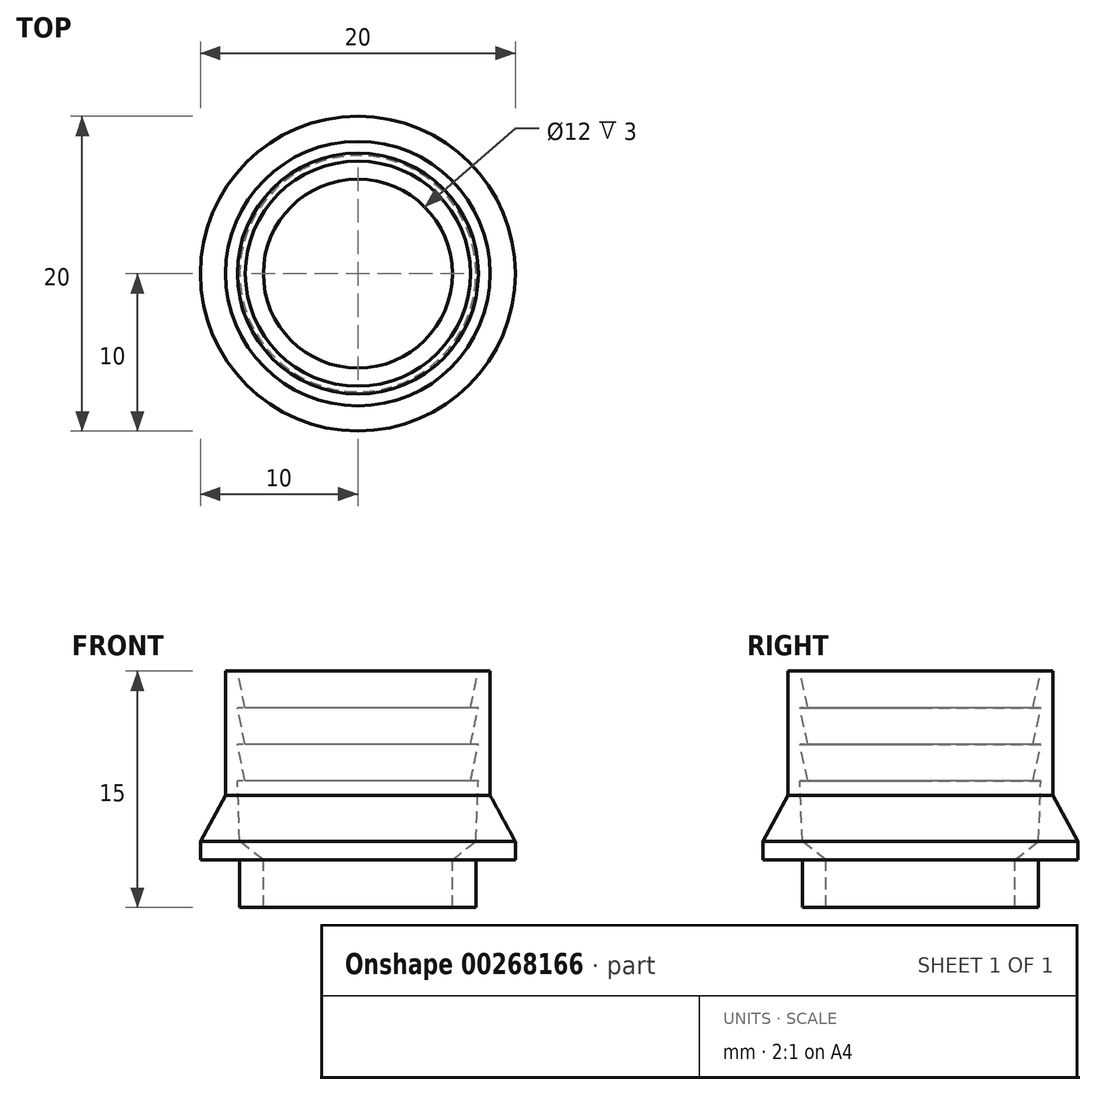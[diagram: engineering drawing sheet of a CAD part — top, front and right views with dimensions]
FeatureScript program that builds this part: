
annotation { "Feature Type Name" : "Feature", "Feature Type Description" : "" }
export const myFeature = defineFeature(function(context is Context, id is Id, definition is map)
    precondition{}
    {
        {
            var Q0;
            Q0=qCreatedBy(makeId("Top.planeOp"),FACE);
            var sketch = newSketch(context, id + "F0", { "sketchPlane" : qUnion([Q0])});
            skCircle(sketch, "E0", {"center": v(0, 0) * mm, "radius": 2.5 * mm});
            skCircle(sketch, "E1", {"center": v(0, 0) * mm, "radius": 4 * mm});
            skCircle(sketch, "E2", {"center": v(0, 0) * mm, "radius": 6 * mm});
            skCircle(sketch, "E3", {"center": v(0, 0) * mm, "radius": 7.5 * mm});
            skSolve(sketch);
        }
        {
            var Q0;
            Q0=qCreatedBy(makeId("Front.planeOp"),FACE);
            var sketch = newSketch(context, id + "F1", { "sketchPlane" : qUnion([Q0])});
            skLineSegment(sketch, "E4", {"start": v(-7.65, 12) * mm, "end": v(-7.15, 9.67) * mm});
            skLineSegment(sketch, "E5", {"start": v(-7.15, 9.67) * mm, "end": v(-7.65, 9.67) * mm});
            skLineSegment(sketch, "E6", {"start": v(-7.65, 9.67) * mm, "end": v(-7.15, 7.35) * mm});
            skLineSegment(sketch, "E7", {"start": v(-7.15, 7.35) * mm, "end": v(-7.65, 7.35) * mm});
            skLineSegment(sketch, "E8", {"start": v(-7.65, 7.35) * mm, "end": v(-7.15, 5.02) * mm});
            skLineSegment(sketch, "E9", {"start": v(-7.15, 5.02) * mm, "end": v(-7.65, 5.02) * mm});
            skLineSegment(sketch, "E10", {"start": v(-7.65, 5.02) * mm, "end": v(-7.5, 1.2) * mm});
            skLineSegment(sketch, "E11", {"start": v(0, 13.24) * mm, "end": v(0, 0) * mm});
            skLineSegment(sketch, "E12", {"start": v(0, 1.2) * mm, "end": v(0, 12) * mm});
            skLineSegment(sketch, "E13", {"start": v(-7.65, 12) * mm, "end": v(-8.4, 12) * mm});
            skLineSegment(sketch, "E14", {"start": v(-10, 1.2) * mm, "end": v(-10, 0) * mm});
            skLineSegment(sketch, "E15", {"start": v(-10, 0) * mm, "end": v(-7.5, 0) * mm});
            skLineSegment(sketch, "E16", {"start": v(-7.5, 0) * mm, "end": v(-7.5, -3) * mm});
            skLineSegment(sketch, "E17", {"start": v(-7.5, -3) * mm, "end": v(-6, -3) * mm});
            skLineSegment(sketch, "E18", {"start": v(-6, -3) * mm, "end": v(-6, 0) * mm});
            skLineSegment(sketch, "E19", {"start": v(-6, 0) * mm, "end": v(-7.5, 1.2) * mm});
            skLineSegment(sketch, "E20", {"start": v(-7.5, 16.3) * mm, "end": v(-7.5, -4.92) * mm, "construction": true});
            skLineSegment(sketch, "E21", {"start": v(-10, 1.2) * mm, "end": v(-8.4, 4.12) * mm});
            skLineSegment(sketch, "E22", {"start": v(-8.4, 4.12) * mm, "end": v(-8.4, 12) * mm});
            skSolve(sketch);
        }
        {
            var Q0;
            Q0=qSketchRegion(id+"F1",true);
            var Q1;
            Q1=sQuery(id+"F1.wireOp",EDGE,"E11");
            revolve(context, id + "F2", {"entities" : qUnion([Q0]), "axis" : qUnion([Q1]), "revolveType" : RevolveType.FULL});
        }
    });
